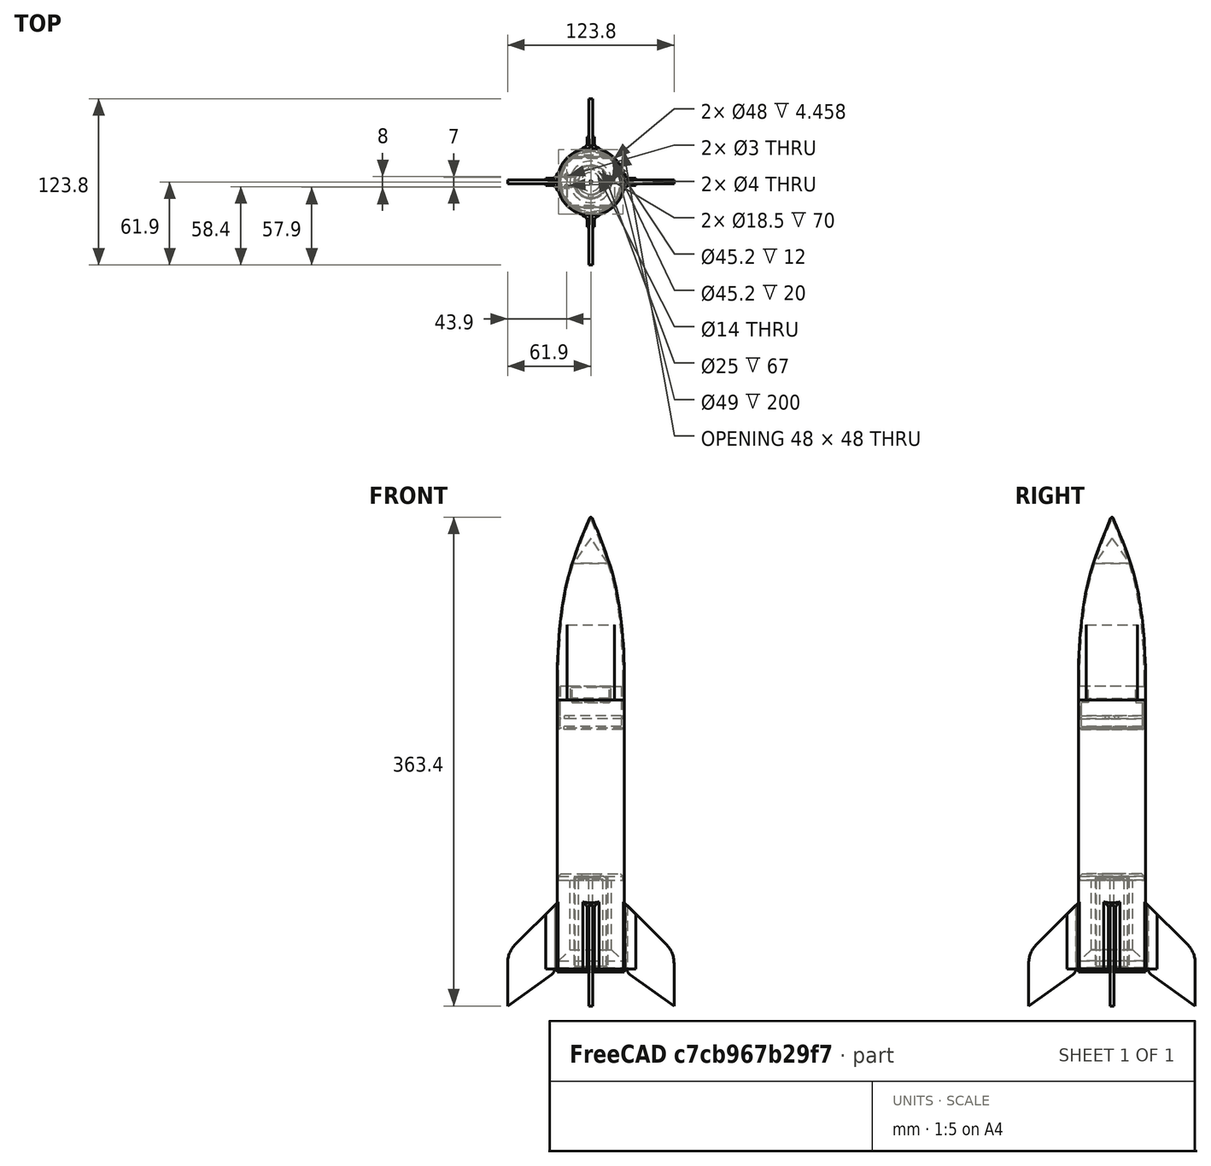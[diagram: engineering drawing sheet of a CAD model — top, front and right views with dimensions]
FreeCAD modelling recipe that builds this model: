
FCSTD DOCUMENT  (FreeCAD 0.21R33694 (Git))
Label: LaMule_V2
License: All rights reserved
LicenseURL: http://en.wikipedia.org/wiki/All_rights_reserved
objects: Sketcher::SketchObject×34, PartDesign::Pad×22, PartDesign::Body×17, PartDesign::Fillet×12, PartDesign::Chamfer×9, PartDesign::Pocket×8, Mesh::Feature×5, PartDesign::Revolution×4, App::LinkGroup×2, PartDesign::Thickness×2, TechDraw::DrawSVGTemplate×1, TechDraw::DrawViewPart×1, TechDraw::DrawPage×1
note: 165 computed .brp shape members not serialized (recipe doc carries the construction recipe); baked Part::Feature solids carry a one-line shape summary decoded from their .brp

FEATURE [Sketcher::SketchObject] Sketch
  FullyConstrained = true
  MapMode = 5
  Placement = pos=(0,0,0) rot=(1,0,0;1.5708rad)
  Support = -> [XZ_Plane]
  sketch-geometry (12):
    g0: LineSegment StartX=24 StartY=0 StartZ=0 EndX=7 EndY=0 EndZ=0
    g1: LineSegment StartX=7 StartY=0 StartZ=0 EndX=7 EndY=3 EndZ=0
    g2: LineSegment StartX=7 StartY=3 StartZ=0 EndX=12.5 EndY=3 EndZ=0
    g3: LineSegment StartX=12.5 StartY=3 StartZ=0 EndX=12.5 EndY=73 EndZ=0
    g4: LineSegment StartX=12.5 StartY=73 StartZ=0 EndX=25 EndY=73 EndZ=0
    g5: LineSegment StartX=25 StartY=73 StartZ=0 EndX=25 EndY=71 EndZ=0
    g6: LineSegment StartX=25 StartY=71 StartZ=0 EndX=24 EndY=70 EndZ=0
    g7: LineSegment StartX=24 StartY=70 StartZ=0 EndX=24 EndY=65 EndZ=0
    g8: LineSegment StartX=24 StartY=65 StartZ=0 EndX=15.5 EndY=56.5 EndZ=0
    g9: LineSegment StartX=15.5 StartY=56.5 StartZ=0 EndX=15.5 EndY=5 EndZ=0
    g10: LineSegment StartX=15.5 StartY=5 StartZ=0 EndX=24 EndY=5 EndZ=0
    g11: LineSegment StartX=24 StartY=5 StartZ=0 EndX=24 EndY=0 EndZ=0
  constraints (36):
    c: PointOnObject(g0,g-1)
    c: PointOnObject(g0,g-1)
    c: Coincident(g0,g1)
    c: Vertical(g1)
    c: Coincident(g1,g2)
    c: Horizontal(g2)
    c: Coincident(g2,g3)
    c: Vertical(g3)
    c: Coincident(g3,g4)
    c: Horizontal(g4)
    c: Coincident(g4,g5)
    c: Coincident(g5,g6)
    c: Coincident(g6,g7)
    c: Vertical(g7)
    c: Coincident(g7,g8)
    c: Coincident(g8,g9)
    c: Vertical(g9)
    c: Coincident(g9,g10)
    c: Horizontal(g10)
    c: Coincident(g10,g11)
    c: Coincident(g11,g0)
    c: DistanceX(g-2,g2) = 12.5
    c: DistanceY(g3,g3) = 70
    c: DistanceY(g1,g1) = 3
    c: DistanceX(g-2,g4) = 25
    c: Vertical(g5)
    c: DistanceY(g5,g5) = 2
    c: DistanceY(g7,g7) = 5
    c: DistanceX(g-1,g0) = 24
    c: DistanceX(g-2,g7) = 24
    c: Distance(g9,g3) = 3
    c: DistanceY(g11,g11) = 5
    c: Angle(g9,g8) = 2.35619
    c: Angle(g7,g6) = 2.35619
    c: Vertical(g11)
    c: DistanceX(g-2,g0) = 7
FEATURE [PartDesign::Revolution] Revolution
  Angle = 360
  Axis = (0,2e-16,1)
  Base = (0,0,0)
  Placement = pos=(0,0,0) rot=(1,0,0;1.5708rad)
  Profile = -> Sketch
  ReferenceAxis = -> Sketch [V_Axis]
  Reversed = true
FEATURE [PartDesign::Chamfer] Chamfer
  Angle = 45
  Base = -> Revolution [Edge6]
  BaseFeature = -> Revolution
  ChamferType = 0
  FlipDirection = false
  Placement = pos=(0,0,0) rot=(1,0,0;1.5708rad)
  Size = 3
  Size2 = 1
  SupportTransform = false
  UseAllEdges = false
FEATURE [PartDesign::Chamfer] Chamfer001
  Angle = 45
  Base = -> Chamfer [Edge12]
  BaseFeature = -> Chamfer
  ChamferType = 0
  FlipDirection = false
  Placement = pos=(0,0,0) rot=(1,0,0;1.5708rad)
  Size = 2
  Size2 = 1
  SupportTransform = false
  UseAllEdges = false
FEATURE [PartDesign::Body] Body  label="support_moteur_V1"
  Group = -> [Sketch,Revolution,Chamfer,Chamfer001]
  Origin = -> Origin
  Placement = pos=(7e-15,0,71) rot=(0,1,0;3.14159rad)
  Tip = -> Chamfer001
FEATURE [Sketcher::SketchObject] Sketch001
  FullyConstrained = true
  MapMode = 5
  Support = -> [XY_Plane001]
  sketch-geometry (2):
    g0: Circle CenterX=0 CenterY=0 CenterZ=0 NormalX=0 NormalY=0 NormalZ=1 AngleXU=0 Radius=24.5
    g1: Circle CenterX=0 CenterY=0 CenterZ=0 NormalX=0 NormalY=0 NormalZ=1 AngleXU=0 Radius=25
  constraints (4):
    c: Radius(g0) = 24.5
    c: Radius(g1) = 25
    c: Coincident(g0,g-1)
    c: Coincident(g1,g0)
FEATURE [PartDesign::Pad] Pad
  Direction = (1,1,1)
  Length = 200
  Length2 = 100
  Profile = -> Sketch001
  Type = 0
FEATURE [PartDesign::Body] Body001  label="tube_V1"
  Group = -> [Sketch001,Pad]
  Origin = -> Origin001
  Tip = -> Pad
FEATURE [Sketcher::SketchObject] Sketch002
  FullyConstrained = true
  MapMode = 5
  Support = -> [XY_Plane002]
  sketch-geometry (12):
    g0: ArcOfCircle CenterX=0 CenterY=0 CenterZ=0 NormalX=0 NormalY=0 NormalZ=1 AngleXU=0 Radius=25 StartAngle=6.04082 EndAngle=6.52555
    g1: LineSegment StartX=24.2693 StartY=-6 StartZ=0 EndX=25.2982 EndY=-6 EndZ=0
    g2: LineSegment StartX=24.2693 StartY=6 StartZ=0 EndX=25.2982 EndY=6 EndZ=0
    g3: LineSegment StartX=25.8697 StartY=2.6 StartZ=0 EndX=33.4517 EndY=2.6 EndZ=0
    g4: LineSegment StartX=33.4517 StartY=2.6 StartZ=0 EndX=33.4517 EndY=1.6 EndZ=0
    g5: LineSegment StartX=33.4517 StartY=1.6 StartZ=0 EndX=26.4517 EndY=1.6 EndZ=0
    g6: LineSegment StartX=26.4517 StartY=1.6 StartZ=0 EndX=26.4517 EndY=-1.6 EndZ=0
    g7: LineSegment StartX=26.4517 StartY=-1.6 StartZ=0 EndX=33.4517 EndY=-1.6 EndZ=0
    g8: LineSegment StartX=33.4517 StartY=-1.6 StartZ=0 EndX=33.4517 EndY=-2.6 EndZ=0
    g9: LineSegment StartX=33.4517 StartY=-2.6 StartZ=0 EndX=25.8697 EndY=-2.6 EndZ=0
    g10: ArcOfCircle CenterX=0 CenterY=0 CenterZ=0 NormalX=0 NormalY=0 NormalZ=1 AngleXU=0 Radius=26 StartAngle=6.05032 EndAngle=6.18302
    g11: ArcOfCircle CenterX=0 CenterY=0 CenterZ=0 NormalX=0 NormalY=0 NormalZ=1 AngleXU=0 Radius=26 StartAngle=0.100167 EndAngle=0.232868
  constraints (33):
    c: Coincident(g0,g-1)
    c: Radius(g0) = 25
    c: Coincident(g0,g1)
    c: Coincident(g0,g2)
    c: Horizontal(g3)
    c: Coincident(g3,g4)
    c: Coincident(g4,g5)
    c: Horizontal(g5)
    c: Coincident(g5,g6)
    c: Coincident(g6,g7)
    c: Horizontal(g7)
    c: Coincident(g7,g8)
    c: Coincident(g8,g9)
    c: Horizontal(g9)
    c: Coincident(g10,g0)
    c: Coincident(g10,g1)
    c: Coincident(g10,g9)
    c: Coincident(g11,g0)
    c: Coincident(g11,g2)
    c: Coincident(g11,g3)
    c: Radius(g11) = 26
    c: Horizontal(g2)
    c: Horizontal(g1)
    c: Symmetric(g7,g4,g-1)
    c: Vertical(g8)
    c: Vertical(g6)
    c: Distance(g6,g5) = 3.2
    c: DistanceY(g4,g4) = 1
    c: Distance(g5,g0) = 26.5
    c: Symmetric(g3,g8,g-1)
    c: DistanceX(g5,g5) = 7
    c: Symmetric(g2,g1,g-1)
    c: DistanceY(g-1,g2) = 6
FEATURE [PartDesign::Pad] Pad001
  Direction = (1,1,1)
  Length = 50
  Length2 = 100
  Profile = -> Sketch002
  Type = 0
FEATURE [PartDesign::Fillet] Fillet
  Base = -> Pad001 [Edge20,Edge1]
  BaseFeature = -> Pad001
  Radius = 4
  SupportTransform = false
  UseAllEdges = false
FEATURE [Sketcher::SketchObject] Sketch003
  ExternalGeometry = -> [Fillet]
  FullyConstrained = true
  MapMode = 5
  Placement = pos=(0,-2.6,0) rot=(1,0,0;1.5708rad)
  Support = -> [Fillet]
  sketch-geometry (3):
    g0: LineSegment StartX=33.4517 StartY=50 StartZ=0 EndX=33.4517 EndY=40.8177 EndZ=0
    g1: LineSegment StartX=33.4517 StartY=40.8177 StartZ=0 EndX=24.2693 EndY=50 EndZ=0
    g2: LineSegment StartX=24.2693 StartY=50 StartZ=0 EndX=33.4517 EndY=50 EndZ=0
  constraints (8):
    c: Coincident(g-4,g0)
    c: PointOnObject(g0,g-4)
    c: Coincident(g0,g1)
    c: PointOnObject(g1,g-3)
    c: Coincident(g1,g2)
    c: Coincident(g2,g0)
    c: Horizontal(g2)
    c: Angle(g1,g2) = 0.785398
FEATURE [PartDesign::Pocket] Pocket
  BaseFeature = -> Fillet
  Direction = (1,1,1)
  Length = 23
  Length2 = 100
  Midplane = true
  Profile = -> Sketch003
  Type = 1
FEATURE [PartDesign::Body] Body002  label="support_aileron_V1"
  Group = -> [Sketch002,Pad001,Fillet,Sketch003,Pocket]
  Origin = -> Origin002
  Tip = -> Pocket
FEATURE [Sketcher::SketchObject] Sketch004
  FullyConstrained = true
  MapMode = 5
  Support = -> [XY_Plane003]
  sketch-geometry (12):
    g0: ArcOfCircle CenterX=0 CenterY=0 CenterZ=0 NormalX=0 NormalY=0 NormalZ=1 AngleXU=0 Radius=25 StartAngle=6.04082 EndAngle=6.52555
    g1: LineSegment StartX=24.2693 StartY=-6 StartZ=0 EndX=25.2982 EndY=-6 EndZ=0
    g2: LineSegment StartX=24.2693 StartY=6 StartZ=0 EndX=25.2982 EndY=6 EndZ=0
    g3: LineSegment StartX=25.8697 StartY=2.6 StartZ=0 EndX=33.4517 EndY=2.6 EndZ=0
    g4: LineSegment StartX=33.4517 StartY=2.6 StartZ=0 EndX=33.4517 EndY=1.6 EndZ=0
    g5: LineSegment StartX=33.4517 StartY=1.6 StartZ=0 EndX=26.4517 EndY=1.6 EndZ=0
    g6: LineSegment StartX=26.4517 StartY=1.6 StartZ=0 EndX=26.4517 EndY=-1.6 EndZ=0
    g7: LineSegment StartX=26.4517 StartY=-1.6 StartZ=0 EndX=33.4517 EndY=-1.6 EndZ=0
    g8: LineSegment StartX=33.4517 StartY=-1.6 StartZ=0 EndX=33.4517 EndY=-2.6 EndZ=0
    g9: LineSegment StartX=33.4517 StartY=-2.6 StartZ=0 EndX=25.8697 EndY=-2.6 EndZ=0
    g10: ArcOfCircle CenterX=0 CenterY=0 CenterZ=0 NormalX=0 NormalY=0 NormalZ=1 AngleXU=0 Radius=26 StartAngle=6.05032 EndAngle=6.18302
    g11: ArcOfCircle CenterX=0 CenterY=0 CenterZ=0 NormalX=0 NormalY=0 NormalZ=1 AngleXU=0 Radius=26 StartAngle=0.100167 EndAngle=0.232868
  constraints (33):
    c: Coincident(g0,g-1)
    c: Radius(g0) = 25
    c: Coincident(g0,g1)
    c: Coincident(g0,g2)
    c: Horizontal(g3)
    c: Coincident(g3,g4)
    c: Coincident(g4,g5)
    c: Horizontal(g5)
    c: Coincident(g5,g6)
    c: Coincident(g6,g7)
    c: Horizontal(g7)
    c: Coincident(g7,g8)
    c: Coincident(g8,g9)
    c: Horizontal(g9)
    c: Coincident(g10,g0)
    c: Coincident(g10,g1)
    c: Coincident(g10,g9)
    c: Coincident(g11,g0)
    c: Coincident(g11,g2)
    c: Coincident(g11,g3)
    c: Radius(g11) = 26
    c: Horizontal(g2)
    c: Horizontal(g1)
    c: Symmetric(g7,g4,g-1)
    c: Vertical(g8)
    c: Vertical(g6)
    c: Distance(g6,g5) = 3.2
    c: DistanceY(g4,g4) = 1
    c: Distance(g5,g0) = 26.5
    c: Symmetric(g3,g8,g-1)
    c: DistanceX(g5,g5) = 7
    c: Symmetric(g2,g1,g-1)
    c: DistanceY(g-1,g2) = 6
FEATURE [PartDesign::Pad] Pad002
  Direction = (1,1,1)
  Length = 50
  Length2 = 100
  Profile = -> Sketch004
  Type = 0
FEATURE [PartDesign::Fillet] Fillet001
  Base = -> Pad002 [Edge20,Edge1]
  BaseFeature = -> Pad002
  Radius = 4
  SupportTransform = false
  UseAllEdges = false
FEATURE [Sketcher::SketchObject] Sketch005
  ExternalGeometry = -> [Fillet001]
  FullyConstrained = true
  MapMode = 5
  Placement = pos=(0,-2.6,0) rot=(1,0,0;1.5708rad)
  Support = -> [Fillet001]
  sketch-geometry (3):
    g0: LineSegment StartX=33.4517 StartY=50 StartZ=0 EndX=33.4517 EndY=40.8177 EndZ=0
    g1: LineSegment StartX=33.4517 StartY=40.8177 StartZ=0 EndX=24.2693 EndY=50 EndZ=0
    g2: LineSegment StartX=24.2693 StartY=50 StartZ=0 EndX=33.4517 EndY=50 EndZ=0
  constraints (8):
    c: Coincident(g-4,g0)
    c: PointOnObject(g0,g-4)
    c: Coincident(g0,g1)
    c: PointOnObject(g1,g-3)
    c: Coincident(g1,g2)
    c: Coincident(g2,g0)
    c: Horizontal(g2)
    c: Angle(g1,g2) = 0.785398
FEATURE [PartDesign::Pocket] Pocket001
  BaseFeature = -> Fillet001
  Direction = (1,1,1)
  Length = 23
  Length2 = 100
  Midplane = true
  Profile = -> Sketch005
  Type = 1
FEATURE [PartDesign::Body] Body003  label="support_aileron_V002"
  Group = -> [Sketch004,Pad002,Fillet001,Sketch005,Pocket001]
  Origin = -> Origin003
  Placement = pos=(0,0,0) rot=(0,0,1;1.5708rad)
  Tip = -> Pocket001
FEATURE [Sketcher::SketchObject] Sketch006
  FullyConstrained = true
  MapMode = 5
  Support = -> [XY_Plane004]
  sketch-geometry (12):
    g0: ArcOfCircle CenterX=0 CenterY=0 CenterZ=0 NormalX=0 NormalY=0 NormalZ=1 AngleXU=0 Radius=25 StartAngle=6.04082 EndAngle=6.52555
    g1: LineSegment StartX=24.2693 StartY=-6 StartZ=0 EndX=25.2982 EndY=-6 EndZ=0
    g2: LineSegment StartX=24.2693 StartY=6 StartZ=0 EndX=25.2982 EndY=6 EndZ=0
    g3: LineSegment StartX=25.8697 StartY=2.6 StartZ=0 EndX=33.4517 EndY=2.6 EndZ=0
    g4: LineSegment StartX=33.4517 StartY=2.6 StartZ=0 EndX=33.4517 EndY=1.6 EndZ=0
    g5: LineSegment StartX=33.4517 StartY=1.6 StartZ=0 EndX=26.4517 EndY=1.6 EndZ=0
    g6: LineSegment StartX=26.4517 StartY=1.6 StartZ=0 EndX=26.4517 EndY=-1.6 EndZ=0
    g7: LineSegment StartX=26.4517 StartY=-1.6 StartZ=0 EndX=33.4517 EndY=-1.6 EndZ=0
    g8: LineSegment StartX=33.4517 StartY=-1.6 StartZ=0 EndX=33.4517 EndY=-2.6 EndZ=0
    g9: LineSegment StartX=33.4517 StartY=-2.6 StartZ=0 EndX=25.8697 EndY=-2.6 EndZ=0
    g10: ArcOfCircle CenterX=0 CenterY=0 CenterZ=0 NormalX=0 NormalY=0 NormalZ=1 AngleXU=0 Radius=26 StartAngle=6.05032 EndAngle=6.18302
    g11: ArcOfCircle CenterX=0 CenterY=0 CenterZ=0 NormalX=0 NormalY=0 NormalZ=1 AngleXU=0 Radius=26 StartAngle=0.100167 EndAngle=0.232868
  constraints (33):
    c: Coincident(g0,g-1)
    c: Radius(g0) = 25
    c: Coincident(g0,g1)
    c: Coincident(g0,g2)
    c: Horizontal(g3)
    c: Coincident(g3,g4)
    c: Coincident(g4,g5)
    c: Horizontal(g5)
    c: Coincident(g5,g6)
    c: Coincident(g6,g7)
    c: Horizontal(g7)
    c: Coincident(g7,g8)
    c: Coincident(g8,g9)
    c: Horizontal(g9)
    c: Coincident(g10,g0)
    c: Coincident(g10,g1)
    c: Coincident(g10,g9)
    c: Coincident(g11,g0)
    c: Coincident(g11,g2)
    c: Coincident(g11,g3)
    c: Radius(g11) = 26
    c: Horizontal(g2)
    c: Horizontal(g1)
    c: Symmetric(g7,g4,g-1)
    c: Vertical(g8)
    c: Vertical(g6)
    c: Distance(g6,g5) = 3.2
    c: DistanceY(g4,g4) = 1
    c: Distance(g5,g0) = 26.5
    c: Symmetric(g3,g8,g-1)
    c: DistanceX(g5,g5) = 7
    c: Symmetric(g2,g1,g-1)
    c: DistanceY(g-1,g2) = 6
FEATURE [PartDesign::Pad] Pad003
  Direction = (1,1,1)
  Length = 50
  Length2 = 100
  Profile = -> Sketch006
  Type = 0
FEATURE [PartDesign::Fillet] Fillet002
  Base = -> Pad003 [Edge20,Edge1]
  BaseFeature = -> Pad003
  Radius = 4
  SupportTransform = false
  UseAllEdges = false
FEATURE [Sketcher::SketchObject] Sketch007
  ExternalGeometry = -> [Fillet002]
  FullyConstrained = true
  MapMode = 5
  Placement = pos=(0,-2.6,0) rot=(1,0,0;1.5708rad)
  Support = -> [Fillet002]
  sketch-geometry (3):
    g0: LineSegment StartX=33.4517 StartY=50 StartZ=0 EndX=33.4517 EndY=40.8177 EndZ=0
    g1: LineSegment StartX=33.4517 StartY=40.8177 StartZ=0 EndX=24.2693 EndY=50 EndZ=0
    g2: LineSegment StartX=24.2693 StartY=50 StartZ=0 EndX=33.4517 EndY=50 EndZ=0
  constraints (8):
    c: Coincident(g-4,g0)
    c: PointOnObject(g0,g-4)
    c: Coincident(g0,g1)
    c: PointOnObject(g1,g-3)
    c: Coincident(g1,g2)
    c: Coincident(g2,g0)
    c: Horizontal(g2)
    c: Angle(g1,g2) = 0.785398
FEATURE [PartDesign::Pocket] Pocket002
  BaseFeature = -> Fillet002
  Direction = (1,1,1)
  Length = 23
  Length2 = 100
  Midplane = true
  Profile = -> Sketch007
  Type = 1
FEATURE [PartDesign::Body] Body004  label="support_aileron_V003"
  Group = -> [Sketch006,Pad003,Fillet002,Sketch007,Pocket002]
  Origin = -> Origin004
  Placement = pos=(0,0,0) rot=(0,0,1;3.14159rad)
  Tip = -> Pocket002
FEATURE [Sketcher::SketchObject] Sketch008
  FullyConstrained = true
  MapMode = 5
  Support = -> [XY_Plane005]
  sketch-geometry (12):
    g0: ArcOfCircle CenterX=0 CenterY=0 CenterZ=0 NormalX=0 NormalY=0 NormalZ=1 AngleXU=0 Radius=25 StartAngle=6.04082 EndAngle=6.52555
    g1: LineSegment StartX=24.2693 StartY=-6 StartZ=0 EndX=25.2982 EndY=-6 EndZ=0
    g2: LineSegment StartX=24.2693 StartY=6 StartZ=0 EndX=25.2982 EndY=6 EndZ=0
    g3: LineSegment StartX=25.8697 StartY=2.6 StartZ=0 EndX=33.4517 EndY=2.6 EndZ=0
    g4: LineSegment StartX=33.4517 StartY=2.6 StartZ=0 EndX=33.4517 EndY=1.6 EndZ=0
    g5: LineSegment StartX=33.4517 StartY=1.6 StartZ=0 EndX=26.4517 EndY=1.6 EndZ=0
    g6: LineSegment StartX=26.4517 StartY=1.6 StartZ=0 EndX=26.4517 EndY=-1.6 EndZ=0
    g7: LineSegment StartX=26.4517 StartY=-1.6 StartZ=0 EndX=33.4517 EndY=-1.6 EndZ=0
    g8: LineSegment StartX=33.4517 StartY=-1.6 StartZ=0 EndX=33.4517 EndY=-2.6 EndZ=0
    g9: LineSegment StartX=33.4517 StartY=-2.6 StartZ=0 EndX=25.8697 EndY=-2.6 EndZ=0
    g10: ArcOfCircle CenterX=0 CenterY=0 CenterZ=0 NormalX=0 NormalY=0 NormalZ=1 AngleXU=0 Radius=26 StartAngle=6.05032 EndAngle=6.18302
    g11: ArcOfCircle CenterX=0 CenterY=0 CenterZ=0 NormalX=0 NormalY=0 NormalZ=1 AngleXU=0 Radius=26 StartAngle=0.100167 EndAngle=0.232868
  constraints (33):
    c: Coincident(g0,g-1)
    c: Radius(g0) = 25
    c: Coincident(g0,g1)
    c: Coincident(g0,g2)
    c: Horizontal(g3)
    c: Coincident(g3,g4)
    c: Coincident(g4,g5)
    c: Horizontal(g5)
    c: Coincident(g5,g6)
    c: Coincident(g6,g7)
    c: Horizontal(g7)
    c: Coincident(g7,g8)
    c: Coincident(g8,g9)
    c: Horizontal(g9)
    c: Coincident(g10,g0)
    c: Coincident(g10,g1)
    c: Coincident(g10,g9)
    c: Coincident(g11,g0)
    c: Coincident(g11,g2)
    c: Coincident(g11,g3)
    c: Radius(g11) = 26
    c: Horizontal(g2)
    c: Horizontal(g1)
    c: Symmetric(g7,g4,g-1)
    c: Vertical(g8)
    c: Vertical(g6)
    c: Distance(g6,g5) = 3.2
    c: DistanceY(g4,g4) = 1
    c: Distance(g5,g0) = 26.5
    c: Symmetric(g3,g8,g-1)
    c: DistanceX(g5,g5) = 7
    c: Symmetric(g2,g1,g-1)
    c: DistanceY(g-1,g2) = 6
FEATURE [PartDesign::Pad] Pad004
  Direction = (1,1,1)
  Length = 50
  Length2 = 100
  Profile = -> Sketch008
  Type = 0
FEATURE [PartDesign::Fillet] Fillet003
  Base = -> Pad004 [Edge20,Edge1]
  BaseFeature = -> Pad004
  Radius = 4
  SupportTransform = false
  UseAllEdges = false
FEATURE [Sketcher::SketchObject] Sketch009
  ExternalGeometry = -> [Fillet003]
  FullyConstrained = true
  MapMode = 5
  Placement = pos=(0,-2.6,0) rot=(1,0,0;1.5708rad)
  Support = -> [Fillet003]
  sketch-geometry (3):
    g0: LineSegment StartX=33.4517 StartY=50 StartZ=0 EndX=33.4517 EndY=40.8177 EndZ=0
    g1: LineSegment StartX=33.4517 StartY=40.8177 StartZ=0 EndX=24.2693 EndY=50 EndZ=0
    g2: LineSegment StartX=24.2693 StartY=50 StartZ=0 EndX=33.4517 EndY=50 EndZ=0
  constraints (8):
    c: Coincident(g-4,g0)
    c: PointOnObject(g0,g-4)
    c: Coincident(g0,g1)
    c: PointOnObject(g1,g-3)
    c: Coincident(g1,g2)
    c: Coincident(g2,g0)
    c: Horizontal(g2)
    c: Angle(g1,g2) = 0.785398
FEATURE [PartDesign::Pocket] Pocket003
  BaseFeature = -> Fillet003
  Direction = (1,1,1)
  Length = 23
  Length2 = 100
  Midplane = true
  Profile = -> Sketch009
  Type = 1
FEATURE [PartDesign::Body] Body005  label="support_aileron_V004"
  Group = -> [Sketch008,Pad004,Fillet003,Sketch009,Pocket003]
  Origin = -> Origin005
  Placement = pos=(0,0,0) rot=(0,0,-1;1.5708rad)
  Tip = -> Pocket003
FEATURE [App::LinkGroup] LinkGroup  label="support_ailerons_V1"
  ElementList = -> [Body005,Body004,Body003,Body002]
  LinkMode = 0
FEATURE [Sketcher::SketchObject] Sketch010
  FullyConstrained = true
  MapMode = 5
  Placement = pos=(0,0,0) rot=(0.57735,0.57735,0.57735;2.0944rad)
  Support = -> [YZ_Plane006]
  sketch-geometry (4):
    g0: LineSegment StartX=27 StartY=-2.5 StartZ=0 EndX=61.9 EndY=-27.4 EndZ=0
    g1: LineSegment StartX=61.9 StartY=-27.4 StartZ=0 EndX=61.9 EndY=12.6 EndZ=0
    g2: LineSegment StartX=61.9 StartY=12.6 StartZ=0 EndX=27 EndY=47.5 EndZ=0
    g3: LineSegment StartX=27 StartY=47.5 StartZ=0 EndX=27 EndY=-2.5 EndZ=0
  constraints (12):
    c: Coincident(g0,g1)
    c: Vertical(g1)
    c: Coincident(g1,g2)
    c: Coincident(g2,g3)
    c: Coincident(g3,g0)
    c: Vertical(g3)
    c: DistanceY(g3,g3) = 50
    c: DistanceY(g-1,g2) = 47.5
    c: DistanceX(g-2,g0) = 27
    c: Angle(g3,g2) = 0.785398
    c: DistanceY(g1,g1) = 40
    c: DistanceX(g-2,g0) = 61.9
FEATURE [PartDesign::Pad] Pad005
  Direction = (1,1,1)
  Length = 3
  Length2 = 100
  Midplane = true
  Placement = pos=(0,0,0) rot=(0.57735,0.57735,0.57735;2.0944rad)
  Profile = -> Sketch010
  Type = 0
FEATURE [PartDesign::Fillet] Fillet004
  Base = -> Pad005 [Edge5]
  BaseFeature = -> Pad005
  Placement = pos=(0,0,0) rot=(0.57735,0.57735,0.57735;2.0944rad)
  Radius = 20
  SupportTransform = false
  UseAllEdges = false
FEATURE [PartDesign::Fillet] Fillet005
  Base = -> Fillet004 [Edge11]
  BaseFeature = -> Fillet004
  Placement = pos=(0,0,0) rot=(0.57735,0.57735,0.57735;2.0944rad)
  Radius = 5
  SupportTransform = false
  UseAllEdges = false
FEATURE [PartDesign::Body] Body006  label="ailerons_V1"
  Group = -> [Sketch010,Pad005,Fillet004,Fillet005]
  Origin = -> Origin006
  Tip = -> Fillet005
FEATURE [Sketcher::SketchObject] Sketch011
  FullyConstrained = true
  MapMode = 5
  Placement = pos=(0,0,0) rot=(0.57735,0.57735,0.57735;2.0944rad)
  Support = -> [YZ_Plane007]
  sketch-geometry (4):
    g0: LineSegment StartX=27 StartY=-2.5 StartZ=0 EndX=61.9 EndY=-27.4 EndZ=0
    g1: LineSegment StartX=61.9 StartY=-27.4 StartZ=0 EndX=61.9 EndY=12.6 EndZ=0
    g2: LineSegment StartX=61.9 StartY=12.6 StartZ=0 EndX=27 EndY=47.5 EndZ=0
    g3: LineSegment StartX=27 StartY=47.5 StartZ=0 EndX=27 EndY=-2.5 EndZ=0
  constraints (12):
    c: Coincident(g0,g1)
    c: Vertical(g1)
    c: Coincident(g1,g2)
    c: Coincident(g2,g3)
    c: Coincident(g3,g0)
    c: Vertical(g3)
    c: DistanceY(g3,g3) = 50
    c: DistanceY(g-1,g2) = 47.5
    c: DistanceX(g-2,g0) = 27
    c: Angle(g3,g2) = 0.785398
    c: DistanceY(g1,g1) = 40
    c: DistanceX(g-2,g0) = 61.9
FEATURE [PartDesign::Pad] Pad006
  Direction = (1,1,1)
  Length = 3
  Length2 = 100
  Midplane = true
  Placement = pos=(0,0,0) rot=(0.57735,0.57735,0.57735;2.0944rad)
  Profile = -> Sketch011
  Type = 0
FEATURE [PartDesign::Fillet] Fillet006
  Base = -> Pad006 [Edge5]
  BaseFeature = -> Pad006
  Placement = pos=(0,0,0) rot=(0.57735,0.57735,0.57735;2.0944rad)
  Radius = 20
  SupportTransform = false
  UseAllEdges = false
FEATURE [PartDesign::Fillet] Fillet007
  Base = -> Fillet006 [Edge11]
  BaseFeature = -> Fillet006
  Placement = pos=(0,0,0) rot=(0.57735,0.57735,0.57735;2.0944rad)
  Radius = 5
  SupportTransform = false
  UseAllEdges = false
FEATURE [PartDesign::Body] Body007  label="ailerons_V002"
  Group = -> [Sketch011,Pad006,Fillet006,Fillet007]
  Origin = -> Origin007
  Placement = pos=(0,0,0) rot=(0,0,1;3.14159rad)
  Tip = -> Fillet007
FEATURE [Sketcher::SketchObject] Sketch012
  FullyConstrained = true
  MapMode = 5
  Placement = pos=(0,0,0) rot=(0.57735,0.57735,0.57735;2.0944rad)
  Support = -> [YZ_Plane008]
  sketch-geometry (4):
    g0: LineSegment StartX=27 StartY=-2.5 StartZ=0 EndX=61.9 EndY=-27.4 EndZ=0
    g1: LineSegment StartX=61.9 StartY=-27.4 StartZ=0 EndX=61.9 EndY=12.6 EndZ=0
    g2: LineSegment StartX=61.9 StartY=12.6 StartZ=0 EndX=27 EndY=47.5 EndZ=0
    g3: LineSegment StartX=27 StartY=47.5 StartZ=0 EndX=27 EndY=-2.5 EndZ=0
  constraints (12):
    c: Coincident(g0,g1)
    c: Vertical(g1)
    c: Coincident(g1,g2)
    c: Coincident(g2,g3)
    c: Coincident(g3,g0)
    c: Vertical(g3)
    c: DistanceY(g3,g3) = 50
    c: DistanceY(g-1,g2) = 47.5
    c: DistanceX(g-2,g0) = 27
    c: Angle(g3,g2) = 0.785398
    c: DistanceY(g1,g1) = 40
    c: DistanceX(g-2,g0) = 61.9
FEATURE [PartDesign::Pad] Pad007
  Direction = (1,1,1)
  Length = 3
  Length2 = 100
  Midplane = true
  Placement = pos=(0,0,0) rot=(0.57735,0.57735,0.57735;2.0944rad)
  Profile = -> Sketch012
  Type = 0
FEATURE [PartDesign::Fillet] Fillet008
  Base = -> Pad007 [Edge5]
  BaseFeature = -> Pad007
  Placement = pos=(0,0,0) rot=(0.57735,0.57735,0.57735;2.0944rad)
  Radius = 20
  SupportTransform = false
  UseAllEdges = false
FEATURE [PartDesign::Fillet] Fillet009
  Base = -> Fillet008 [Edge11]
  BaseFeature = -> Fillet008
  Placement = pos=(0,0,0) rot=(0.57735,0.57735,0.57735;2.0944rad)
  Radius = 5
  SupportTransform = false
  UseAllEdges = false
FEATURE [PartDesign::Body] Body008  label="ailerons_V003"
  Group = -> [Sketch012,Pad007,Fillet008,Fillet009]
  Origin = -> Origin008
  Placement = pos=(0,0,0) rot=(0,0,1;1.5708rad)
  Tip = -> Fillet009
FEATURE [Sketcher::SketchObject] Sketch013
  FullyConstrained = true
  MapMode = 5
  Placement = pos=(0,0,0) rot=(0.57735,0.57735,0.57735;2.0944rad)
  Support = -> [YZ_Plane009]
  sketch-geometry (4):
    g0: LineSegment StartX=27 StartY=-2.5 StartZ=0 EndX=61.9 EndY=-27.4 EndZ=0
    g1: LineSegment StartX=61.9 StartY=-27.4 StartZ=0 EndX=61.9 EndY=12.6 EndZ=0
    g2: LineSegment StartX=61.9 StartY=12.6 StartZ=0 EndX=27 EndY=47.5 EndZ=0
    g3: LineSegment StartX=27 StartY=47.5 StartZ=0 EndX=27 EndY=-2.5 EndZ=0
  constraints (12):
    c: Coincident(g0,g1)
    c: Vertical(g1)
    c: Coincident(g1,g2)
    c: Coincident(g2,g3)
    c: Coincident(g3,g0)
    c: Vertical(g3)
    c: DistanceY(g3,g3) = 50
    c: DistanceY(g-1,g2) = 47.5
    c: DistanceX(g-2,g0) = 27
    c: Angle(g3,g2) = 0.785398
    c: DistanceY(g1,g1) = 40
    c: DistanceX(g-2,g0) = 61.9
FEATURE [PartDesign::Pad] Pad008
  Direction = (1,1,1)
  Length = 3
  Length2 = 100
  Midplane = true
  Placement = pos=(0,0,0) rot=(0.57735,0.57735,0.57735;2.0944rad)
  Profile = -> Sketch013
  Type = 0
FEATURE [PartDesign::Fillet] Fillet010
  Base = -> Pad008 [Edge5]
  BaseFeature = -> Pad008
  Placement = pos=(0,0,0) rot=(0.57735,0.57735,0.57735;2.0944rad)
  Radius = 20
  SupportTransform = false
  UseAllEdges = false
FEATURE [PartDesign::Fillet] Fillet011
  Base = -> Fillet010 [Edge11]
  BaseFeature = -> Fillet010
  Placement = pos=(0,0,0) rot=(0.57735,0.57735,0.57735;2.0944rad)
  Radius = 5
  SupportTransform = false
  UseAllEdges = false
FEATURE [PartDesign::Body] Body009  label="ailerons_V004"
  Group = -> [Sketch013,Pad008,Fillet010,Fillet011]
  Origin = -> Origin009
  Placement = pos=(0,0,0) rot=(0,0,-1;1.5708rad)
  Tip = -> Fillet011
FEATURE [App::LinkGroup] LinkGroup001  label="ailerons"
  ElementList = -> [Body009,Body008,Body007,Body006]
  LinkMode = 0
FEATURE [Sketcher::SketchObject] Sketch014
  FullyConstrained = true
  MapMode = 5
  Support = -> [XY_Plane010]
  sketch-geometry (12):
    g0: LineSegment StartX=0 StartY=0 StartZ=0 EndX=134.73 EndY=0 EndZ=0
    g1: LineSegment StartX=134.73 StartY=-24 StartZ=0 EndX=134.73 EndY=0 EndZ=0
    g2: LineSegment StartX=134.73 StartY=-24 StartZ=0 EndX=120.272 EndY=-24 EndZ=0
    g3-g7: Circle x5 (B-spline internal-alignment scaffolding for g8; pole/knot coordinates omitted)
    g8: BSplineCurve PolesCount=5 KnotsCount=3 Degree=3 IsPeriodic=0
    g9: GeomPoint X=120.272 Y=-24 Z=0
    g10: GeomPoint X=62.1183 Y=-19.6849 Z=0
    g11: GeomPoint X=0 Y=0 Z=0
  constraints (23):
    c: Coincident(g0,g-1)
    c: PointOnObject(g0,g-1)
    c: Coincident(g1,g0)
    c: Vertical(g1)
    c: Coincident(g2,g1)
    c: Horizontal(g2)
    c: Coincident(g8,g2)
    c: Weight(g3) = 1
    c: Equal(g3, g4-g7) x4
    c: Coincident(g8,g0)
    c: InternalAlignment(g3-g7 -> g8) x5
    c: InternalAlignment(g9,g8)
    c: InternalAlignment(g10,g8)
    c: InternalAlignment(g11,g8)
    c: DistanceX(g6) = 33.4091
    c: DistanceY(g6) = -14.1378
    c: DistanceX(g5) = 61.0359
    c: DistanceY(g5) = -20.426
    c: DistanceX(g4) = 92.9923
    c: DistanceY(g4) = -23.75
    c: DistanceX(g2) = 120.272
    c: DistanceY(g2) = -24
    c: DistanceX(g0,g0) = 134.73
FEATURE [PartDesign::Revolution] Revolution001
  Angle = 360
  Axis = (1,0,0)
  Base = (0,0,0)
  Profile = -> Sketch014
  ReferenceAxis = -> X_Axis010
  Reversed = true
FEATURE [PartDesign::Thickness] Thickness
  Base = -> Revolution001 [Face1]
  BaseFeature = -> Revolution001
  Intersection = false
  Join = 0
  Mode = 0
  SupportTransform = false
  Value = 1
FEATURE [Sketcher::SketchObject] Sketch015
  FullyConstrained = true
  MapMode = 5
  Placement = pos=(134.73,0,0) rot=(0.57735,0.57735,0.57735;2.0944rad)
  Support = -> [Thickness]
  sketch-geometry (5):
    g0: Circle CenterX=1.1e-15 CenterY=0 CenterZ=0 NormalX=0 NormalY=0 NormalZ=1 AngleXU=0 Radius=25
    g1: ArcOfCircle CenterX=1.1e-15 CenterY=0 CenterZ=0 NormalX=0 NormalY=0 NormalZ=1 AngleXU=0 Radius=24 StartAngle=0.675132 EndAngle=2.46646
    g2: ArcOfCircle CenterX=1.1e-15 CenterY=0 CenterZ=0 NormalX=0 NormalY=0 NormalZ=1 AngleXU=0 Radius=24 StartAngle=3.81672 EndAngle=5.60805
    g3: LineSegment StartX=-18.735 StartY=15 StartZ=0 EndX=-18.735 EndY=-15 EndZ=0
    g4: LineSegment StartX=18.735 StartY=15 StartZ=0 EndX=18.735 EndY=-15 EndZ=0
  constraints (14):
    c: Coincident(g0,g-1)
    c: Radius(g0) = 25
    c: Coincident(g1,g0)
    c: Coincident(g2,g0)
    c: Symmetric(g2,g2,g-2)
    c: Symmetric(g2,g1,g-1)
    c: Radius(g1) = 24
    c: Equal(g1,g2)
    c: Coincident(g3,g1)
    c: Coincident(g3,g2)
    c: Coincident(g4,g1)
    c: Coincident(g4,g2)
    c: Symmetric(g1,g1,g-2)
    c: DistanceY(g4,g4) = 30
FEATURE [PartDesign::Pad] Pad009
  BaseFeature = -> Thickness
  Direction = (1,1,1)
  Length = 10
  Length2 = 100
  Profile = -> Sketch015
  Reversed = true
  Type = 0
FEATURE [PartDesign::Chamfer] Chamfer002
  Angle = 45
  Base = -> Pad009 [Edge9,Edge6]
  BaseFeature = -> Pad009
  ChamferType = 0
  FlipDirection = false
  Size = 1
  Size2 = 1
  SupportTransform = false
  UseAllEdges = false
FEATURE [PartDesign::Body] Body010  label="coiffe_V1"
  Group = -> [Sketch014,Revolution001,Thickness,Sketch015,Pad009,Chamfer002]
  Origin = -> Origin010
  Placement = pos=(-7.4e-14,0,335) rot=(0,1,0;1.5708rad)
  Tip = -> Chamfer002
FEATURE [Mesh::Feature] Mesh  label="coiffe_V1 (Meshed)"
FEATURE [TechDraw::DrawSVGTemplate] Template
  EditableTexts = Approved1=N/A; Approved2=N/A; CheckedBy=Papas Inventeurs; Code=Code; CompanyAddress=planête Terre, système solaire; CompanyName=Lift Off; DrawingNumber=1; DrawingTitle1=LaMule; DrawingTitle2=Envoyons quelque chose en l'air!; DrawingTitle3="Just because"; DrawnBy=Maël & PéPé; Revision=Rev 1; Scale=Scale; Sheet=Page 1 de 1
  Height = 215.9
  Orientation = 1
  Width = 279.4
FEATURE [TechDraw::DrawViewPart] View001
  CoarseView = false
  Direction = (0.207,0.686,-0.698)
  Focus = 100
  HardHidden = false
  IsoCount = 0
  IsoHidden = false
  IsoVisible = false
  LockPosition = false
  Perspective = false
  Rotation = 0
  Scale = 0.7
  ScaleType = 2
  ScrubCount = 0
  SeamHidden = false
  SeamVisible = true
  SmoothHidden = false
  SmoothVisible = true
  Source = -> [Body,Body001,Body010]
  X = 146.884
  XDirection = (-0.176,0.728,0.663)
  XSource = -> [LinkGroup,LinkGroup001]
  Y = 131.376
FEATURE [TechDraw::DrawPage] Page
  KeepUpdated = true
  NextBalloonIndex = 1
  ProjectionType = 0
  Template = -> Template
  Views = -> [View001]
FEATURE [Sketcher::SketchObject] Sketch016
  FullyConstrained = true
  MapMode = 5
  Support = -> [XY_Plane011]
  sketch-geometry (8):
    g0: ArcOfCircle CenterX=0 CenterY=-2.3e-15 CenterZ=0 NormalX=0 NormalY=0 NormalZ=1 AngleXU=0 Radius=23.8 StartAngle=2.2259 EndAngle=4.05728
    g1: ArcOfCircle CenterX=0 CenterY=-2.3e-15 CenterZ=0 NormalX=0 NormalY=0 NormalZ=1 AngleXU=0 Radius=23.8 StartAngle=5.3675 EndAngle=7.19888
    g2: LineSegment StartX=-14.5 StartY=-18.873 StartZ=0 EndX=14.5 EndY=-18.873 EndZ=0
    g3: LineSegment StartX=-14.5 StartY=18.873 StartZ=0 EndX=14.5 EndY=18.873 EndZ=0
    g4: ArcOfCircle CenterX=0 CenterY=-2.3e-15 CenterZ=0 NormalX=0 NormalY=0 NormalZ=1 AngleXU=0 Radius=22.6 StartAngle=2.22941 EndAngle=4.05377
    g5: ArcOfCircle CenterX=0 CenterY=-2.3e-15 CenterZ=0 NormalX=0 NormalY=0 NormalZ=1 AngleXU=0 Radius=22.6 StartAngle=5.371 EndAngle=7.19537
    g6: LineSegment StartX=-13.8317 StartY=17.873 StartZ=0 EndX=13.8317 EndY=17.873 EndZ=0
    g7: LineSegment StartX=13.8317 StartY=-17.873 StartZ=0 EndX=-13.8317 EndY=-17.873 EndZ=0
  constraints (22):
    c: Coincident(g0,g-1)
    c: Coincident(g0,g1)
    c: Coincident(g0,g2)
    c: Coincident(g1,g2)
    c: Coincident(g1,g3)
    c: Coincident(g0,g3)
    c: Symmetric(g1,g0,g-2)
    c: Symmetric(g0,g1,g-2)
    c: Radius(g1) = 23.8
    c: Symmetric(g0,g0,g-1)
    c: DistanceX(g2,g2) = 29
    c: Coincident(g4,g0)
    c: Coincident(g5,g0)
    c: Coincident(g6,g4)
    c: Coincident(g6,g5)
    c: Coincident(g7,g5)
    c: Coincident(g7,g4)
    c: Symmetric(g5,g5,g-1)
    c: Symmetric(g5,g4,g-2)
    c: Radius(g5) = 22.6
    c: Horizontal(g7)
    c: Distance(g4,g3) = 1
FEATURE [PartDesign::Pad] Pad010
  Direction = (1,1,1)
  Length = 10
  Length2 = 100
  Profile = -> Sketch016
  Type = 0
FEATURE [PartDesign::Chamfer] Chamfer003
  Angle = 45
  Base = -> Pad010 [Edge7,Edge12]
  BaseFeature = -> Pad010
  ChamferType = 0
  FlipDirection = false
  Size = 0.5
  Size2 = 1
  SupportTransform = false
  UseAllEdges = false
FEATURE [Sketcher::SketchObject] Sketch017
  FullyConstrained = true
  MapMode = 5
  Placement = pos=(0,0,0) rot=(1,0,0;3.14159rad)
  Support = -> [Chamfer003]
  sketch-geometry (2):
    g0: Circle CenterX=0 CenterY=0 CenterZ=0 NormalX=0 NormalY=0 NormalZ=1 AngleXU=0 Radius=23.9
    g1: Circle CenterX=0 CenterY=0 CenterZ=0 NormalX=0 NormalY=0 NormalZ=1 AngleXU=0 Radius=22.6
  constraints (4):
    c: Coincident(g0,g-1)
    c: Radius(g0) = 23.9
    c: Coincident(g1,g0)
    c: Radius(g1) = 22.6
FEATURE [PartDesign::Pad] Pad011
  BaseFeature = -> Chamfer003
  Direction = (1,1,1)
  Length = 20
  Length2 = 100
  Profile = -> Sketch017
  Type = 0
FEATURE [Sketcher::SketchObject] Sketch018
  ExternalGeometry = -> [Pad011]
  FullyConstrained = true
  MapMode = 5
  Placement = pos=(0,0,0) rot=(1,0,0;3.14159rad)
  Support = -> [Pad011]
  sketch-geometry (4):
    g0: ArcOfCircle CenterX=-1.1e-15 CenterY=0 CenterZ=0 NormalX=0 NormalY=0 NormalZ=1 AngleXU=0 Radius=23.9 StartAngle=3.98637 EndAngle=5.43841
    g1: ArcOfCircle CenterX=-1.1e-15 CenterY=0 CenterZ=0 NormalX=0 NormalY=0 NormalZ=1 AngleXU=0 Radius=23.9 StartAngle=0.844779 EndAngle=2.29681
    g2: LineSegment StartX=-15.8671 StartY=17.873 StartZ=0 EndX=15.8671 EndY=17.873 EndZ=0
    g3: LineSegment StartX=-15.8671 StartY=-17.873 StartZ=0 EndX=15.8671 EndY=-17.873 EndZ=0
  constraints (14):
    c: Coincident(g0,g-1)
    c: PointOnObject(g0,g-3)
    c: PointOnObject(g0,g-3)
    c: Coincident(g1,g0)
    c: PointOnObject(g1,g-3)
    c: PointOnObject(g1,g-3)
    c: Coincident(g2,g1)
    c: Coincident(g2,g1)
    c: Horizontal(g2)
    c: PointOnObject(g-4,g2)
    c: Coincident(g3,g0)
    c: Coincident(g3,g0)
    c: Horizontal(g3)
    c: PointOnObject(g-5,g3)
FEATURE [PartDesign::Pad] Pad012
  BaseFeature = -> Pad011
  Direction = (1,1,1)
  Length = 2
  Length2 = 100
  Profile = -> Sketch018
  Type = 0
FEATURE [Sketcher::SketchObject] Sketch019
  ExternalGeometry = -> [Pad012]
  FullyConstrained = true
  MapMode = 5
  Placement = pos=(0,0,-20) rot=(1,0,0;3.14159rad)
  Support = -> [Pad012]
  sketch-geometry (3):
    g0: Circle CenterX=-18 CenterY=4 CenterZ=0 NormalX=0 NormalY=0 NormalZ=1 AngleXU=0 Radius=1.5
    g1: Circle CenterX=-18 CenterY=-4 CenterZ=0 NormalX=0 NormalY=0 NormalZ=1 AngleXU=0 Radius=1.5
    g2: Circle CenterX=0 CenterY=0 CenterZ=0 NormalX=0 NormalY=0 NormalZ=1 AngleXU=0 Radius=23.9
  constraints (7):
    c: Radius(g1) = 1.5
    c: Equal(g1,g0)
    c: Symmetric(g0,g1,g-1)
    c: DistanceX(g0) = -18
    c: DistanceY(g0) = 4
    c: Radius(g2) = 23.9
    c: Coincident(g2,g-1)
FEATURE [PartDesign::Pad] Pad013
  BaseFeature = -> Pad012
  Direction = (1,1,1)
  Length = 2
  Length2 = 100
  Profile = -> Sketch019
  Type = 0
FEATURE [PartDesign::Chamfer] Chamfer004
  Angle = 45
  Base = -> Pad013 [Edge42]
  BaseFeature = -> Pad013
  ChamferType = 0
  FlipDirection = false
  Size = 1
  Size2 = 1
  SupportTransform = false
  UseAllEdges = false
FEATURE [PartDesign::Body] Body011  label="couvercle_coiffe_V1"
  Group = -> [Sketch016,Pad010,Chamfer003,Sketch017,Pad011,Sketch018,Pad012,Sketch019,Pad013,Chamfer004]
  Origin = -> Origin011
  Placement = pos=(0,0,200.3) rot=(0,0,1;0rad)
  Tip = -> Chamfer004
FEATURE [Mesh::Feature] Mesh001  label="couvercle_coiffe_V1 (Meshed)"
FEATURE [Sketcher::SketchObject] Sketch020
  FullyConstrained = true
  MapMode = 5
  Support = -> [XY_Plane012]
  sketch-geometry (2):
    g0: Circle CenterX=0 CenterY=0 CenterZ=0 NormalX=0 NormalY=0 NormalZ=1 AngleXU=0 Radius=9.25
    g1: Circle CenterX=0 CenterY=0 CenterZ=0 NormalX=0 NormalY=0 NormalZ=1 AngleXU=0 Radius=11.75
  constraints (4):
    c: Coincident(g0,g-1)
    c: Coincident(g1,g0)
    c: Radius(g1) = 11.75
    c: Radius(g0) = 9.25
FEATURE [PartDesign::Pad] Pad014
  Direction = (1,1,1)
  Length = 70
  Length2 = 100
  Profile = -> Sketch020
  Type = 0
FEATURE [Sketcher::SketchObject] Sketch021
  FullyConstrained = true
  MapMode = 5
  Placement = pos=(0,0,0) rot=(1,0,0;3.14159rad)
  Support = -> [Pad014]
  sketch-geometry (4):
    g0: LineSegment StartX=-15.74 StartY=1.5 StartZ=0 EndX=15.74 EndY=1.5 EndZ=0
    g1: LineSegment StartX=15.74 StartY=1.5 StartZ=0 EndX=15.74 EndY=-1.5 EndZ=0
    g2: LineSegment StartX=15.74 StartY=-1.5 StartZ=0 EndX=-15.74 EndY=-1.5 EndZ=0
    g3: LineSegment StartX=-15.74 StartY=-1.5 StartZ=0 EndX=-15.74 EndY=1.5 EndZ=0
  constraints (11):
    c: Coincident(g0,g1)
    c: Coincident(g1,g2)
    c: Coincident(g2,g3)
    c: Coincident(g3,g0)
    c: Horizontal(g0)
    c: Horizontal(g2)
    c: Vertical(g1)
    c: Vertical(g3)
    c: Symmetric(g1,g0,g-1)
    c: DistanceX(g2,g2) = 31.48
    c: DistanceY(g1,g1) = 3
FEATURE [PartDesign::Pocket] Pocket004
  BaseFeature = -> Pad014
  Direction = (1,1,1)
  Length = 67
  Length2 = 100
  Profile = -> Sketch021
  Type = 0
FEATURE [PartDesign::Chamfer] Chamfer005
  Angle = 45
  Base = -> Pocket004 [Edge3,Edge7]
  BaseFeature = -> Pocket004
  ChamferType = 0
  FlipDirection = false
  Size = 2
  Size2 = 1
  SupportTransform = false
  UseAllEdges = false
FEATURE [Sketcher::SketchObject] Sketch022
  FullyConstrained = true
  MapMode = 5
  Placement = pos=(0,0,0) rot=(1,0,0;3.14159rad)
  Support = -> [Chamfer005]
  sketch-geometry (4):
    g0: LineSegment StartX=-1.5 StartY=15.795 StartZ=0 EndX=1.5 EndY=15.795 EndZ=0
    g1: LineSegment StartX=1.5 StartY=15.795 StartZ=0 EndX=1.5 EndY=-15.795 EndZ=0
    g2: LineSegment StartX=1.5 StartY=-15.795 StartZ=0 EndX=-1.5 EndY=-15.795 EndZ=0
    g3: LineSegment StartX=-1.5 StartY=-15.795 StartZ=0 EndX=-1.5 EndY=15.795 EndZ=0
  constraints (11):
    c: Coincident(g0,g1)
    c: Coincident(g1,g2)
    c: Coincident(g2,g3)
    c: Coincident(g3,g0)
    c: Horizontal(g0)
    c: Horizontal(g2)
    c: Vertical(g1)
    c: Vertical(g3)
    c: Symmetric(g1,g0,g-1)
    c: DistanceX(g2,g2) = 3
    c: DistanceY(g1,g1) = 31.59
FEATURE [PartDesign::Pocket] Pocket005
  BaseFeature = -> Chamfer005
  Direction = (1,1,1)
  Length = 67
  Length2 = 100
  Profile = -> Sketch022
  Type = 0
FEATURE [PartDesign::Body] Body012  label="Adaptateur_moteur_V1"
  Group = -> [Sketch020,Pad014,Sketch021,Pocket004,Chamfer005,Sketch022,Pocket005]
  Origin = -> Origin012
  Placement = pos=(0,8e-15,69) rot=(1,0,0;3.14159rad)
  Tip = -> Pocket005
FEATURE [Mesh::Feature] Mesh002  label="couvercle_coiffe_V1 (Meshed)001"
FEATURE [Sketcher::SketchObject] Sketch023
  FullyConstrained = true
  MapMode = 5
  Support = -> [XY_Plane013]
  sketch-geometry (2):
    g0: Circle CenterX=0 CenterY=0 CenterZ=0 NormalX=0 NormalY=0 NormalZ=1 AngleXU=0 Radius=9.25
    g1: Circle CenterX=0 CenterY=0 CenterZ=0 NormalX=0 NormalY=0 NormalZ=1 AngleXU=0 Radius=11.75
  constraints (4):
    c: Coincident(g0,g-1)
    c: Coincident(g1,g0)
    c: Radius(g1) = 11.75
    c: Radius(g0) = 9.25
FEATURE [PartDesign::Pad] Pad015
  Direction = (1,1,1)
  Length = 70
  Length2 = 100
  Profile = -> Sketch023
  Type = 0
FEATURE [Sketcher::SketchObject] Sketch025
  FullyConstrained = true
  MapMode = 5
  Placement = pos=(0,0,0) rot=(1,0,0;3.14159rad)
  Support = -> [Pad015]
  sketch-geometry (4):
    g0: LineSegment StartX=-15.74 StartY=1.5 StartZ=0 EndX=15.74 EndY=1.5 EndZ=0
    g1: LineSegment StartX=15.74 StartY=1.5 StartZ=0 EndX=15.74 EndY=-1.5 EndZ=0
    g2: LineSegment StartX=15.74 StartY=-1.5 StartZ=0 EndX=-15.74 EndY=-1.5 EndZ=0
    g3: LineSegment StartX=-15.74 StartY=-1.5 StartZ=0 EndX=-15.74 EndY=1.5 EndZ=0
  constraints (11):
    c: Coincident(g0,g1)
    c: Coincident(g1,g2)
    c: Coincident(g2,g3)
    c: Coincident(g3,g0)
    c: Horizontal(g0)
    c: Horizontal(g2)
    c: Vertical(g1)
    c: Vertical(g3)
    c: Symmetric(g1,g0,g-1)
    c: DistanceX(g2,g2) = 31.48
    c: DistanceY(g1,g1) = 3
FEATURE [PartDesign::Pocket] Pocket007
  BaseFeature = -> Pad015
  Direction = (1,1,1)
  Length = 67
  Length2 = 100
  Profile = -> Sketch025
  Type = 0
FEATURE [PartDesign::Chamfer] Chamfer006
  Angle = 45
  Base = -> Pocket007 [Edge3,Edge7]
  BaseFeature = -> Pocket007
  ChamferType = 0
  FlipDirection = false
  Size = 2
  Size2 = 1
  SupportTransform = false
  UseAllEdges = false
FEATURE [Sketcher::SketchObject] Sketch024
  ExternalGeometry = -> [Chamfer006]
  FullyConstrained = true
  MapMode = 5
  Placement = pos=(0,0,0) rot=(1,0,0;3.14159rad)
  Support = -> [Chamfer006]
  sketch-geometry (8):
    g0: LineSegment StartX=-1.5 StartY=13.94 StartZ=0 EndX=11.6539 EndY=13.94 EndZ=0
    g1: LineSegment StartX=11.6539 StartY=13.94 StartZ=0 EndX=11.6539 EndY=1.5 EndZ=0
    g2: LineSegment StartX=11.6539 StartY=1.5 StartZ=0 EndX=-1.5 EndY=1.5 EndZ=0
    g3: LineSegment StartX=-1.5 StartY=1.5 StartZ=0 EndX=-1.5 EndY=13.94 EndZ=0
    g4: LineSegment StartX=-11.6539 StartY=-1.5 StartZ=0 EndX=1.5 EndY=-1.5 EndZ=0
    g5: LineSegment StartX=1.5 StartY=-1.5 StartZ=0 EndX=1.5 EndY=-13.94 EndZ=0
    g6: LineSegment StartX=1.5 StartY=-13.94 StartZ=0 EndX=-11.6539 EndY=-13.94 EndZ=0
    g7: LineSegment StartX=-11.6539 StartY=-13.94 StartZ=0 EndX=-11.6539 EndY=-1.5 EndZ=0
  constraints (21):
    c: Coincident(g0,g1)
    c: Coincident(g1,g2)
    c: Coincident(g2,g3)
    c: Coincident(g3,g0)
    c: Horizontal(g0)
    c: Horizontal(g2)
    c: Vertical(g1)
    c: Vertical(g3)
    c: Coincident(g1,g-3)
    c: DistanceX(g-2,g0) = -1.5
    c: DistanceY(g1,g1) = 12.44
    c: Coincident(g4,g5)
    c: Coincident(g5,g6)
    c: Coincident(g6,g7)
    c: Coincident(g7,g4)
    c: Horizontal(g4)
    c: Horizontal(g6)
    c: Vertical(g5)
    c: Vertical(g7)
    c: Coincident(g4,g-4)
    c: Symmetric(g5,g0,g-1)
FEATURE [PartDesign::Pocket] Pocket006
  BaseFeature = -> Chamfer006
  Direction = (1,1,1)
  Length = 67
  Length2 = 100
  Profile = -> Sketch024
  Type = 0
FEATURE [PartDesign::Body] Body013  label="Adaptateur_moteur_V2"
  Group = -> [Sketch023,Pad015,Sketch025,Pocket007,Chamfer006,Sketch024,Pocket006]
  Origin = -> Origin013
  Placement = pos=(0,8e-15,69) rot=(1,0,0;3.14159rad)
  Tip = -> Pocket006
FEATURE [Sketcher::SketchObject] Sketch026
  FullyConstrained = true
  MapMode = 5
  Placement = pos=(0,0,0) rot=(0.57735,0.57735,0.57735;2.0944rad)
  Support = -> [YZ_Plane014]
  sketch-geometry (4):
    g0: LineSegment StartX=19 StartY=0 StartZ=0 EndX=-19 EndY=0 EndZ=0
    g1: LineSegment StartX=-19 StartY=0 StartZ=0 EndX=-19 EndY=55 EndZ=0
    g2: LineSegment StartX=-19 StartY=55 StartZ=0 EndX=19 EndY=55 EndZ=0
    g3: LineSegment StartX=19 StartY=55 StartZ=0 EndX=19 EndY=0 EndZ=0
  constraints (11):
    c: Coincident(g0,g1)
    c: Coincident(g1,g2)
    c: Coincident(g2,g3)
    c: Coincident(g3,g0)
    c: Horizontal(g0)
    c: Vertical(g1)
    c: Vertical(g3)
    c: PointOnObject(g0,g-1)
    c: Symmetric(g1,g2,g-2)
    c: DistanceX(g2,g2) = 38
    c: DistanceY(g3,g3) = 55
FEATURE [PartDesign::Pad] Pad016
  Direction = (1,-2e-16,3e-16)
  Length = 35
  Length2 = 100
  Midplane = true
  Placement = pos=(0,0,0) rot=(0.57735,0.57735,0.57735;2.0944rad)
  Profile = -> Sketch026
  ReferenceAxis = -> Sketch026 [N_Axis]
  Type = 0
FEATURE [PartDesign::Body] Body014  label="Charge_utile_V2"
  Group = -> [Sketch026,Pad016]
  Origin = -> Origin014
  Placement = pos=(0,0,201) rot=(0,0,1;0rad)
  Tip = -> Pad016
FEATURE [Sketcher::SketchObject] Sketch027
  FullyConstrained = true
  MapMode = 5
  Support = -> [XY_Plane015]
  sketch-geometry (12):
    g0: LineSegment StartX=0 StartY=0 StartZ=0 EndX=134.73 EndY=0 EndZ=0
    g1: LineSegment StartX=134.73 StartY=-24 StartZ=0 EndX=134.73 EndY=0 EndZ=0
    g2: LineSegment StartX=134.73 StartY=-24 StartZ=0 EndX=120.272 EndY=-24 EndZ=0
    g3-g7: Circle x5 (B-spline internal-alignment scaffolding for g8; pole/knot coordinates omitted)
    g8: BSplineCurve PolesCount=5 KnotsCount=3 Degree=3 IsPeriodic=0
    g9: GeomPoint X=120.272 Y=-24 Z=0
    g10: GeomPoint X=62.1183 Y=-19.6849 Z=0
    g11: GeomPoint X=0 Y=0 Z=0
  constraints (23):
    c: Coincident(g0,g-1)
    c: PointOnObject(g0,g-1)
    c: Coincident(g1,g0)
    c: Vertical(g1)
    c: Coincident(g2,g1)
    c: Horizontal(g2)
    c: Coincident(g8,g2)
    c: Weight(g3) = 1
    c: Equal(g3, g4-g7) x4
    c: Coincident(g8,g0)
    c: InternalAlignment(g3-g7 -> g8) x5
    c: InternalAlignment(g9,g8)
    c: InternalAlignment(g10,g8)
    c: InternalAlignment(g11,g8)
    c: DistanceX(g6) = 33.4091
    c: DistanceY(g6) = -14.1378
    c: DistanceX(g5) = 61.0359
    c: DistanceY(g5) = -20.426
    c: DistanceX(g4) = 92.9923
    c: DistanceY(g4) = -23.75
    c: DistanceX(g2) = 120.272
    c: DistanceY(g2) = -24
    c: DistanceX(g0,g0) = 134.73
FEATURE [PartDesign::Revolution] Revolution002
  Angle = 360
  Axis = (1,0,0)
  Base = (0,0,0)
  Profile = -> Sketch027
  ReferenceAxis = -> X_Axis015
  Reversed = true
FEATURE [PartDesign::Thickness] Thickness001
  Base = -> Revolution002 [Face1]
  BaseFeature = -> Revolution002
  Intersection = false
  Join = 0
  Mode = 0
  SupportTransform = false
  Value = 1
FEATURE [Sketcher::SketchObject] Sketch028
  FullyConstrained = true
  MapMode = 5
  Placement = pos=(134.73,0,0) rot=(0.57735,0.57735,0.57735;2.0944rad)
  Support = -> [Thickness001]
  sketch-geometry (5):
    g0: Circle CenterX=1.1e-15 CenterY=0 CenterZ=0 NormalX=0 NormalY=0 NormalZ=1 AngleXU=0 Radius=25
    g1: ArcOfCircle CenterX=1.1e-15 CenterY=0 CenterZ=0 NormalX=0 NormalY=0 NormalZ=1 AngleXU=0 Radius=24 StartAngle=0.675132 EndAngle=2.46646
    g2: ArcOfCircle CenterX=1.1e-15 CenterY=0 CenterZ=0 NormalX=0 NormalY=0 NormalZ=1 AngleXU=0 Radius=24 StartAngle=3.81672 EndAngle=5.60805
    g3: LineSegment StartX=-18.735 StartY=15 StartZ=0 EndX=-18.735 EndY=-15 EndZ=0
    g4: LineSegment StartX=18.735 StartY=15 StartZ=0 EndX=18.735 EndY=-15 EndZ=0
  constraints (14):
    c: Coincident(g0,g-1)
    c: Radius(g0) = 25
    c: Coincident(g1,g0)
    c: Coincident(g2,g0)
    c: Symmetric(g2,g2,g-2)
    c: Symmetric(g2,g1,g-1)
    c: Radius(g1) = 24
    c: Equal(g1,g2)
    c: Coincident(g3,g1)
    c: Coincident(g3,g2)
    c: Coincident(g4,g1)
    c: Coincident(g4,g2)
    c: Symmetric(g1,g1,g-2)
    c: DistanceY(g4,g4) = 30
FEATURE [PartDesign::Pad] Pad017
  BaseFeature = -> Thickness001
  Direction = (1,1,1)
  Length = 10
  Length2 = 100
  Profile = -> Sketch028
  Reversed = true
  Type = 0
FEATURE [PartDesign::Chamfer] Chamfer007
  Angle = 45
  Base = -> Pad017 [Edge9,Edge6]
  BaseFeature = -> Pad017
  ChamferType = 0
  FlipDirection = false
  Size = 1
  Size2 = 1
  SupportTransform = false
  UseAllEdges = false
FEATURE [Sketcher::SketchObject] Sketch029
  FullyConstrained = true
  MapMode = 5
  Support = -> [XY_Plane016]
  sketch-geometry (8):
    g0: ArcOfCircle CenterX=0 CenterY=-2.3e-15 CenterZ=0 NormalX=0 NormalY=0 NormalZ=1 AngleXU=0 Radius=23.8 StartAngle=2.2259 EndAngle=4.05728
    g1: ArcOfCircle CenterX=0 CenterY=-2.3e-15 CenterZ=0 NormalX=0 NormalY=0 NormalZ=1 AngleXU=0 Radius=23.8 StartAngle=5.3675 EndAngle=7.19888
    g2: LineSegment StartX=-14.5 StartY=-18.873 StartZ=0 EndX=14.5 EndY=-18.873 EndZ=0
    g3: LineSegment StartX=-14.5 StartY=18.873 StartZ=0 EndX=14.5 EndY=18.873 EndZ=0
    g4: ArcOfCircle CenterX=0 CenterY=-2.3e-15 CenterZ=0 NormalX=0 NormalY=0 NormalZ=1 AngleXU=0 Radius=22.6 StartAngle=2.22941 EndAngle=4.05377
    g5: ArcOfCircle CenterX=0 CenterY=-2.3e-15 CenterZ=0 NormalX=0 NormalY=0 NormalZ=1 AngleXU=0 Radius=22.6 StartAngle=5.371 EndAngle=7.19537
    g6: LineSegment StartX=-13.8317 StartY=17.873 StartZ=0 EndX=13.8317 EndY=17.873 EndZ=0
    g7: LineSegment StartX=13.8317 StartY=-17.873 StartZ=0 EndX=-13.8317 EndY=-17.873 EndZ=0
  constraints (22):
    c: Coincident(g0,g-1)
    c: Coincident(g0,g1)
    c: Coincident(g0,g2)
    c: Coincident(g1,g2)
    c: Coincident(g1,g3)
    c: Coincident(g0,g3)
    c: Symmetric(g1,g0,g-2)
    c: Symmetric(g0,g1,g-2)
    c: Radius(g1) = 23.8
    c: Symmetric(g0,g0,g-1)
    c: DistanceX(g2,g2) = 29
    c: Coincident(g4,g0)
    c: Coincident(g5,g0)
    c: Coincident(g6,g4)
    c: Coincident(g6,g5)
    c: Coincident(g7,g5)
    c: Coincident(g7,g4)
    c: Symmetric(g5,g5,g-1)
    c: Symmetric(g5,g4,g-2)
    c: Radius(g5) = 22.6
    c: Horizontal(g7)
    c: Distance(g4,g3) = 1
FEATURE [PartDesign::Pad] Pad018
  Direction = (1,1,1)
  Length = 10
  Length2 = 100
  Profile = -> Sketch029
  Type = 0
FEATURE [PartDesign::Chamfer] Chamfer008
  Angle = 45
  Base = -> Pad018 [Edge7,Edge12]
  BaseFeature = -> Pad018
  ChamferType = 0
  FlipDirection = false
  Size = 0.5
  Size2 = 1
  SupportTransform = false
  UseAllEdges = false
FEATURE [Sketcher::SketchObject] Sketch030
  FullyConstrained = true
  MapMode = 5
  Placement = pos=(0,0,0) rot=(1,0,0;3.14159rad)
  Support = -> [Chamfer008]
  sketch-geometry (2):
    g0: Circle CenterX=0 CenterY=0 CenterZ=0 NormalX=0 NormalY=0 NormalZ=1 AngleXU=0 Radius=23.9
    g1: Circle CenterX=0 CenterY=0 CenterZ=0 NormalX=0 NormalY=0 NormalZ=1 AngleXU=0 Radius=22.6
  constraints (4):
    c: Coincident(g0,g-1)
    c: Radius(g0) = 23.9
    c: Coincident(g1,g0)
    c: Radius(g1) = 22.6
FEATURE [PartDesign::Pad] Pad019
  BaseFeature = -> Chamfer008
  Direction = (1,1,1)
  Length = 12
  Length2 = 100
  Profile = -> Sketch030
  Type = 0
FEATURE [Sketcher::SketchObject] Sketch031
  ExternalGeometry = -> [Pad019]
  FullyConstrained = true
  MapMode = 5
  Placement = pos=(0,0,0) rot=(1,0,0;3.14159rad)
  Support = -> [Pad019]
  sketch-geometry (4):
    g0: ArcOfCircle CenterX=-1.1e-15 CenterY=0 CenterZ=0 NormalX=0 NormalY=0 NormalZ=1 AngleXU=0 Radius=23.9 StartAngle=3.98637 EndAngle=5.43841
    g1: ArcOfCircle CenterX=-1.1e-15 CenterY=0 CenterZ=0 NormalX=0 NormalY=0 NormalZ=1 AngleXU=0 Radius=23.9 StartAngle=0.844779 EndAngle=2.29681
    g2: LineSegment StartX=-15.8671 StartY=17.873 StartZ=0 EndX=15.8671 EndY=17.873 EndZ=0
    g3: LineSegment StartX=-15.8671 StartY=-17.873 StartZ=0 EndX=15.8671 EndY=-17.873 EndZ=0
  constraints (14):
    c: Coincident(g0,g-1)
    c: PointOnObject(g0,g-3)
    c: PointOnObject(g0,g-3)
    c: Coincident(g1,g0)
    c: PointOnObject(g1,g-3)
    c: PointOnObject(g1,g-3)
    c: Coincident(g2,g1)
    c: Coincident(g2,g1)
    c: Horizontal(g2)
    c: PointOnObject(g-4,g2)
    c: Coincident(g3,g0)
    c: Coincident(g3,g0)
    c: Horizontal(g3)
    c: PointOnObject(g-5,g3)
FEATURE [PartDesign::Pad] Pad020
  BaseFeature = -> Pad019
  Direction = (1,1,1)
  Length = 2
  Length2 = 100
  Profile = -> Sketch031
  Type = 0
FEATURE [Sketcher::SketchObject] Sketch032
  ExternalGeometry = -> [Pad020]
  FullyConstrained = true
  MapMode = 5
  Placement = pos=(0,0,-12) rot=(1,0,0;3.14159rad)
  Support = -> [Pad020]
  sketch-geometry (3):
    g0: Circle CenterX=0 CenterY=0 CenterZ=0 NormalX=0 NormalY=0 NormalZ=1 AngleXU=0 Radius=23.9
    g1: Circle CenterX=-18 CenterY=3.5 CenterZ=0 NormalX=0 NormalY=0 NormalZ=1 AngleXU=0 Radius=1.5
    g2: Circle CenterX=-18 CenterY=-3.5 CenterZ=0 NormalX=0 NormalY=0 NormalZ=1 AngleXU=0 Radius=1.5
  constraints (8):
    c: Coincident(g0,g-1)
    c: Radius(g-3) = 23.9
    c: Radius(g0) = 23.9
    c: Radius(g2) = 1.5
    c: Equal(g2,g1)
    c: Symmetric(g1,g2,g-1)
    c: DistanceX(g-2,g1) = -18
    c: DistanceY(g-1,g1) = 3.5
FEATURE [PartDesign::Pad] Pad021
  BaseFeature = -> Pad020
  Direction = (1,1,1)
  Length = 2
  Length2 = 100
  Profile = -> Sketch032
  Type = 0
FEATURE [PartDesign::Body] Body016  label="couvercle_coiffe_V002"
  Group = -> [Sketch029,Pad018,Chamfer008,Sketch030,Pad019,Sketch031,Pad020,Sketch032,Pad021]
  Origin = -> Origin016
  Placement = pos=(0,0,200.3) rot=(0,0,1;0rad)
  Tip = -> Pad021
FEATURE [Sketcher::SketchObject] Sketch033
  FullyConstrained = true
  MapMode = 5
  Placement = pos=(0,0,0) rot=(1,0,0;1.5708rad)
  Support = -> [XZ_Plane015]
  sketch-geometry (4):
    g0: LineSegment StartX=-0.5 StartY=0 StartZ=0 EndX=14.5 EndY=0 EndZ=0
    g1: LineSegment StartX=24.4481 StartY=10.14 StartZ=0 EndX=-0.5 EndY=0 EndZ=0
    g2: LineSegment StartX=24.4481 StartY=10.14 StartZ=0 EndX=34.6427 EndY=13.7353 EndZ=0
    g3: LineSegment StartX=34.6427 StartY=13.7353 StartZ=0 EndX=14.5 EndY=0 EndZ=0
  constraints (12):
    c: PointOnObject(g0,g-1)
    c: PointOnObject(g0,g-1)
    c: DistanceX(g0,g0) = 15
    c: DistanceX(g-2,g0) = -0.5
    c: Coincident(g1,g0)
    c: DistanceY(g0,g1) = 10.14
    c: Coincident(g1,g2)
    c: Coincident(g2,g3)
    c: Coincident(g3,g0)
    c: Distance(g3) = 24.38
    c: Distance(g2) = 10.81
    c: Distance(g1) = 26.93
FEATURE [PartDesign::Revolution] Revolution003
  Angle = 360
  Axis = (1,0,0)
  Base = (0,0,0)
  BaseFeature = -> Chamfer007
  Profile = -> Sketch033
  ReferenceAxis = -> Sketch033 [H_Axis]
FEATURE [PartDesign::Body] Body015  label="coiffe_V002"
  Group = -> [Sketch027,Revolution002,Thickness001,Sketch028,Pad017,Chamfer007,Sketch033,Revolution003]
  Origin = -> Origin015
  Placement = pos=(-7.4e-14,0,335) rot=(0,1,0;1.5708rad)
  Tip = -> Revolution003
FEATURE [Mesh::Feature] Mesh003  label="coiffe_V002 (Meshed)"
FEATURE [Mesh::Feature] Mesh004  label="couvercle_coiffe_V002 (Meshed)"
